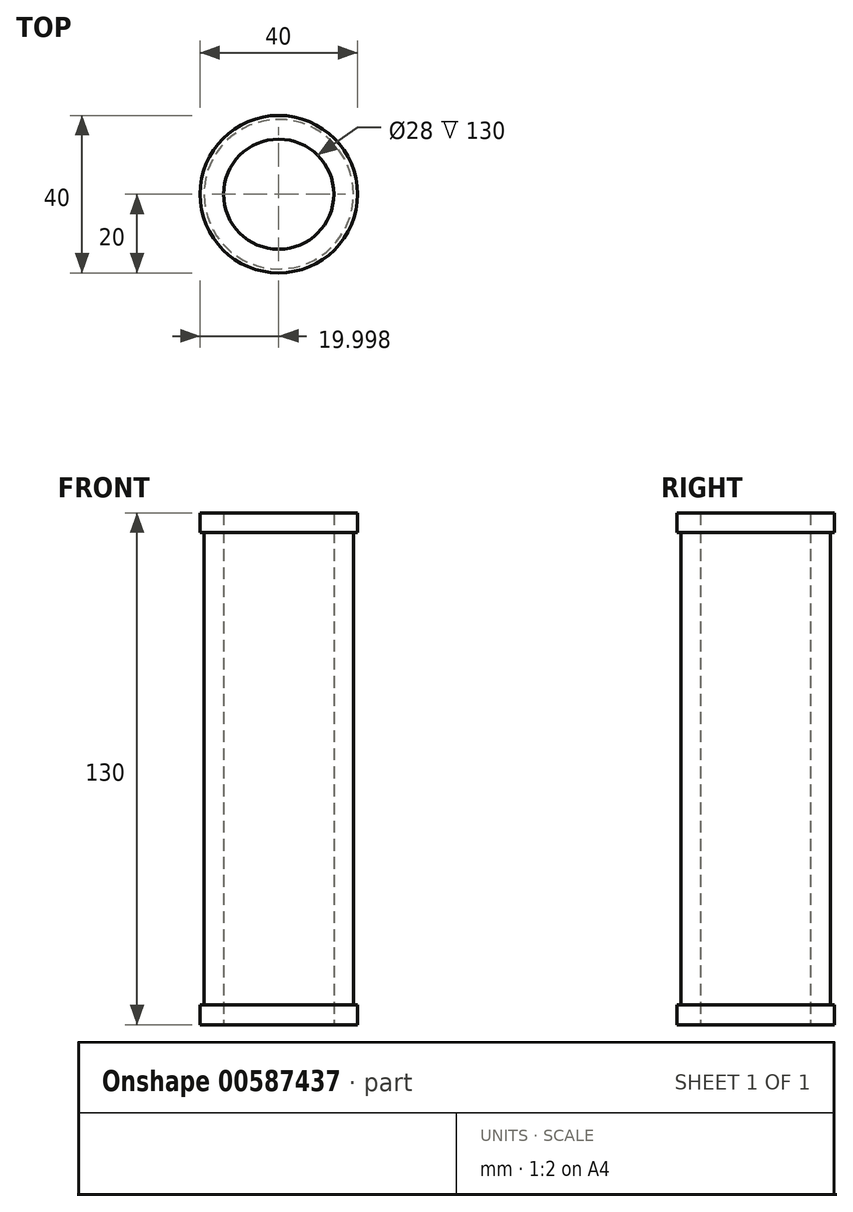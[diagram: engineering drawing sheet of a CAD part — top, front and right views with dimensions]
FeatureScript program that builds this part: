
annotation { "Feature Type Name" : "Feature", "Feature Type Description" : "" }
export const myFeature = defineFeature(function(context is Context, id is Id, definition is map)
    precondition{}
    {
        {
            var Q0;
            Q0=qCreatedBy(makeId("Top.planeOp"),FACE);
            var sketch = newSketch(context, id + "F0", { "sketchPlane" : qUnion([Q0])});
            skCircle(sketch, "E0", {"center": v(-23.14, 0) * mm, "radius": 14 * mm});
            skCircle(sketch, "E1.0", {"center": v(-23.14, 0) * mm, "radius": 20 * mm});
            skPoint(sketch, "E2.endSnap0", {"position": v(-38.2, 5.92) * mm});
            skSolve(sketch);
        }
        {
            var Q0;
            Q0 = qSketchRegion(id + "F0", true);
            extrude(context, id + "F1", {"entities" : qUnion([Q0]), "endBound" : BoundingType.SYMMETRIC, "depth" : 130 * mm, "offsetDistance" : 25 * mm});
        }
        {
            var Q0;
            Q0=makeQuery(id+"F1.opExtrude","SWEPT_FACE",FACE,{"disambiguationData":[OSD([sQuery(id+"F0.wireOp",EDGE,"E1.0")])]});
            shell(context, id + "F2", {"entities" : qUnion([Q0]), "thickness" : 5 * mm});
        }
    });
